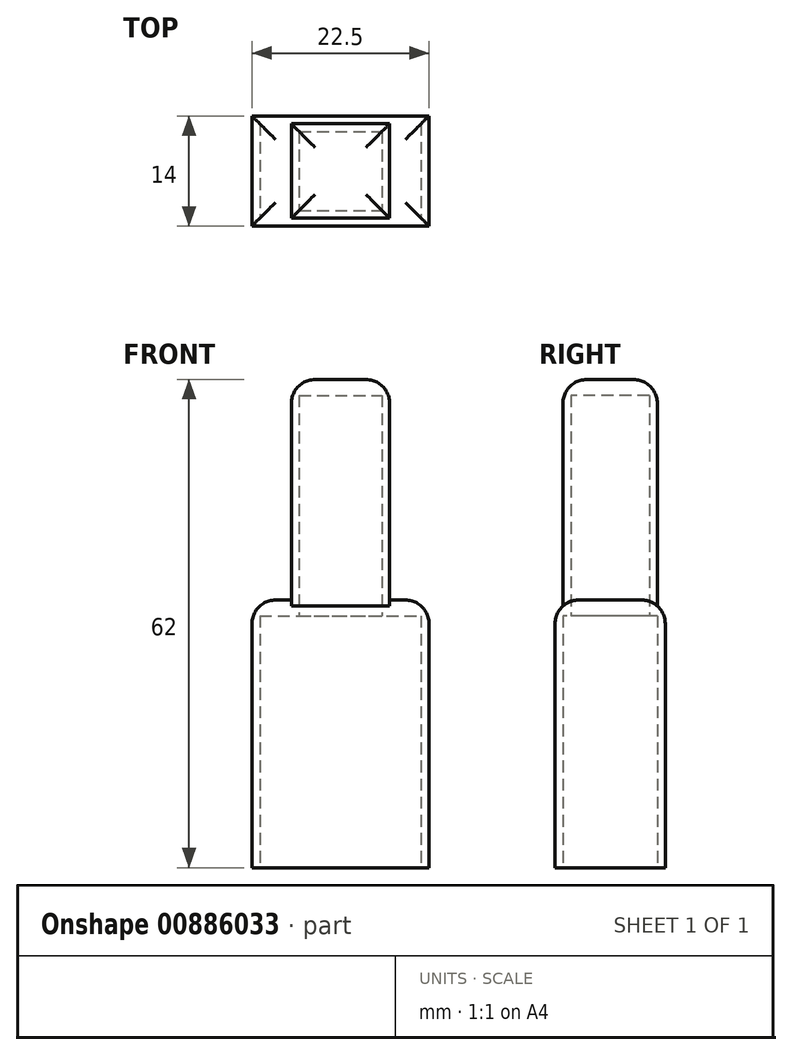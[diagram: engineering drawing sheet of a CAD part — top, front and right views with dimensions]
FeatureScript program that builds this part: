
annotation { "Feature Type Name" : "Feature", "Feature Type Description" : "" }
export const myFeature = defineFeature(function(context is Context, id is Id, definition is map)
    precondition{}
    {
        {
            var Q0;
            Q0=qCreatedBy(makeId("Top.planeOp"),FACE);
            var sketch = newSketch(context, id + "F0", { "sketchPlane" : qUnion([Q0])});
            skLineSegment(sketch, "E0.bottom", {"start": v(-10.25, 6) * mm, "end": v(10.25, 6) * mm});
            skLineSegment(sketch, "E0.top", {"start": v(-10.25, -6) * mm, "end": v(10.25, -6) * mm});
            skLineSegment(sketch, "E0.left", {"start": v(-10.25, 6) * mm, "end": v(-10.25, -6) * mm});
            skLineSegment(sketch, "E0.right", {"start": v(10.25, 6) * mm, "end": v(10.25, -6) * mm});
            skPoint(sketch, "E0.middle", {"position": v(0, 0) * mm});
            skLineSegment(sketch, "E1.bottom", {"start": v(-5.25, 5) * mm, "end": v(5.25, 5) * mm});
            skLineSegment(sketch, "E1.top", {"start": v(-5.25, -5) * mm, "end": v(5.25, -5) * mm});
            skLineSegment(sketch, "E1.left", {"start": v(-5.25, 5) * mm, "end": v(-5.25, -5) * mm});
            skLineSegment(sketch, "E1.right", {"start": v(5.25, 5) * mm, "end": v(5.25, -5) * mm});
            skLineSegment(sketch, "E2.bottom", {"start": v(-11.25, 7) * mm, "end": v(11.25, 7) * mm});
            skLineSegment(sketch, "E2.top", {"start": v(-11.25, -7) * mm, "end": v(11.25, -7) * mm});
            skLineSegment(sketch, "E2.left", {"start": v(-11.25, 7) * mm, "end": v(-11.25, -7) * mm});
            skLineSegment(sketch, "E2.right", {"start": v(11.25, 7) * mm, "end": v(11.25, -7) * mm});
            skLineSegment(sketch, "E3.bottom", {"start": v(-6.25, 6) * mm, "end": v(6.25, 6) * mm});
            skLineSegment(sketch, "E3.top", {"start": v(-6.25, -6) * mm, "end": v(6.25, -6) * mm});
            skLineSegment(sketch, "E3.left", {"start": v(-6.25, 6) * mm, "end": v(-6.25, -6) * mm});
            skLineSegment(sketch, "E3.right", {"start": v(6.25, 6) * mm, "end": v(6.25, -6) * mm});
            skSolve(sketch);
        }
        {
            var Q0;
            Q0=makeQuery(id+"F0.imprint","IMPRINT",FACE,{"disambiguationData":[TD([[makeQuery(id+"F0.imprint","IMPRINT",EDGE,{"derivedFrom":sQuery(id+"F0.wireOp",EDGE,"E1.bottom")}),1.0]])]});
            var Q1;
            Q1=makeQuery(id+"F0.imprint","IMPRINT",FACE,{"disambiguationData":[TD([[makeQuery(id+"F0.imprint","IMPRINT",EDGE,{"derivedFrom":sQuery(id+"F0.wireOp",EDGE,"E1.bottom")}),-1.0]])]});
            extrude(context, id + "F1", {"entities" : qUnion([Q0, Q1]), "depth" : 62 * mm, "offsetDistance" : 25 * mm});
        }
        {
            var Q0;
            {var subQ1=sQuery(id+"F0.wireOp",EDGE,"E0.left");Q0=makeQuery(id+"F0.imprint","IMPRINT",FACE,{"disambiguationData":[TD([[makeQuery(id+"F0.imprint","IMPRINT",EDGE,{"derivedFrom":subQ1}),-1.0]])]});}
            var Q1;
            {var subQ0=sQuery(id+"F0.wireOp",EDGE,"E0.left");Q1=makeQuery(id+"F0.imprint","IMPRINT",FACE,{"disambiguationData":[TD([[makeQuery(id+"F0.imprint","IMPRINT",EDGE,{"derivedFrom":subQ0}),1.0]])]});}
            var Q2;
            {var subQ0=sQuery(id+"F0.wireOp",EDGE,"E0.right");Q2=makeQuery(id+"F0.imprint","IMPRINT",FACE,{"disambiguationData":[TD([[makeQuery(id+"F0.imprint","IMPRINT",EDGE,{"derivedFrom":subQ0}),-1.0]])]});}
            extrude(context, id + "F2", {"entities" : qUnion([Q0, Q1, Q2]), "operationType" : NewBodyOperationType.ADD, "depth" : 34 * mm, "offsetDistance" : 25 * mm});
        }
        {
            var Q0;
            Q0=makeQuery(id+"F0.imprint","IMPRINT",FACE,{"disambiguationData":[TD([[makeQuery(id+"F0.imprint","IMPRINT",EDGE,{"derivedFrom":sQuery(id+"F0.wireOp",EDGE,"E1.bottom")}),-1.0]])]});
            extrude(context, id + "F3", {"entities" : qUnion([Q0]), "operationType" : NewBodyOperationType.REMOVE, "depth" : 60 * mm, "offsetDistance" : 25 * mm});
        }
        {
            var Q0;
            Q0=makeQuery(id+"F0.imprint","IMPRINT",FACE,{"disambiguationData":[TD([[makeQuery(id+"F0.imprint","IMPRINT",EDGE,{"derivedFrom":sQuery(id+"F0.wireOp",EDGE,"E1.bottom")}),1.0]])]});
            var Q1;
            {var subQ0=sQuery(id+"F0.wireOp",EDGE,"E0.left");Q1=makeQuery(id+"F0.imprint","IMPRINT",FACE,{"disambiguationData":[TD([[makeQuery(id+"F0.imprint","IMPRINT",EDGE,{"derivedFrom":subQ0}),1.0]])]});}
            var Q2;
            {var subQ0=sQuery(id+"F0.wireOp",EDGE,"E0.right");Q2=makeQuery(id+"F0.imprint","IMPRINT",FACE,{"disambiguationData":[TD([[makeQuery(id+"F0.imprint","IMPRINT",EDGE,{"derivedFrom":subQ0}),-1.0]])]});}
            extrude(context, id + "F4", {"entities" : qUnion([Q0, Q1, Q2]), "operationType" : NewBodyOperationType.REMOVE, "depth" : 32 * mm, "offsetDistance" : 25 * mm});
        }
        {
            var Q0;
            Q0=makeQuery(id+"F1.opExtrude","CAP_FACE",FACE,{"disambiguationData":[OSD([sQuery(id+"F0.wireOp",EDGE,"E3.bottom"),sQuery(id+"F0.wireOp",EDGE,"E3.top"),sQuery(id+"F0.wireOp",EDGE,"E3.left"),sQuery(id+"F0.wireOp",EDGE,"E3.right")])],"isStart":false});
            fillet(context, id + "F5", {"entities" : qUnion([Q0]), "radius" : 3 * mm, "tangentPropagation" : true, "allowEdgeOverflow" : false});
        }
        {
            var Q0;
            Q0=makeQuery(id+"F2.opExtrude","CAP_EDGE",EDGE,{"disambiguationData":[OSD([sQuery(id+"F0.wireOp",EDGE,"E2.left")])],"isStart":false});
            var Q1;
            Q1=makeQuery(id+"F2.opExtrude","CAP_EDGE",EDGE,{"disambiguationData":[OSD([sQuery(id+"F0.wireOp",EDGE,"E2.top")])],"isStart":false});
            var Q2;
            Q2=makeQuery(id+"F2.opExtrude","CAP_EDGE",EDGE,{"disambiguationData":[OSD([sQuery(id+"F0.wireOp",EDGE,"E2.bottom")])],"isStart":false});
            var Q3;
            Q3=makeQuery(id+"F2.opExtrude","CAP_EDGE",EDGE,{"disambiguationData":[OSD([sQuery(id+"F0.wireOp",EDGE,"E2.right")])],"isStart":false});
            fillet(context, id + "F6", {"entities" : qUnion([Q0, Q1, Q2, Q3]), "radius" : 3 * mm, "tangentPropagation" : true, "allowEdgeOverflow" : false});
        }
    });
